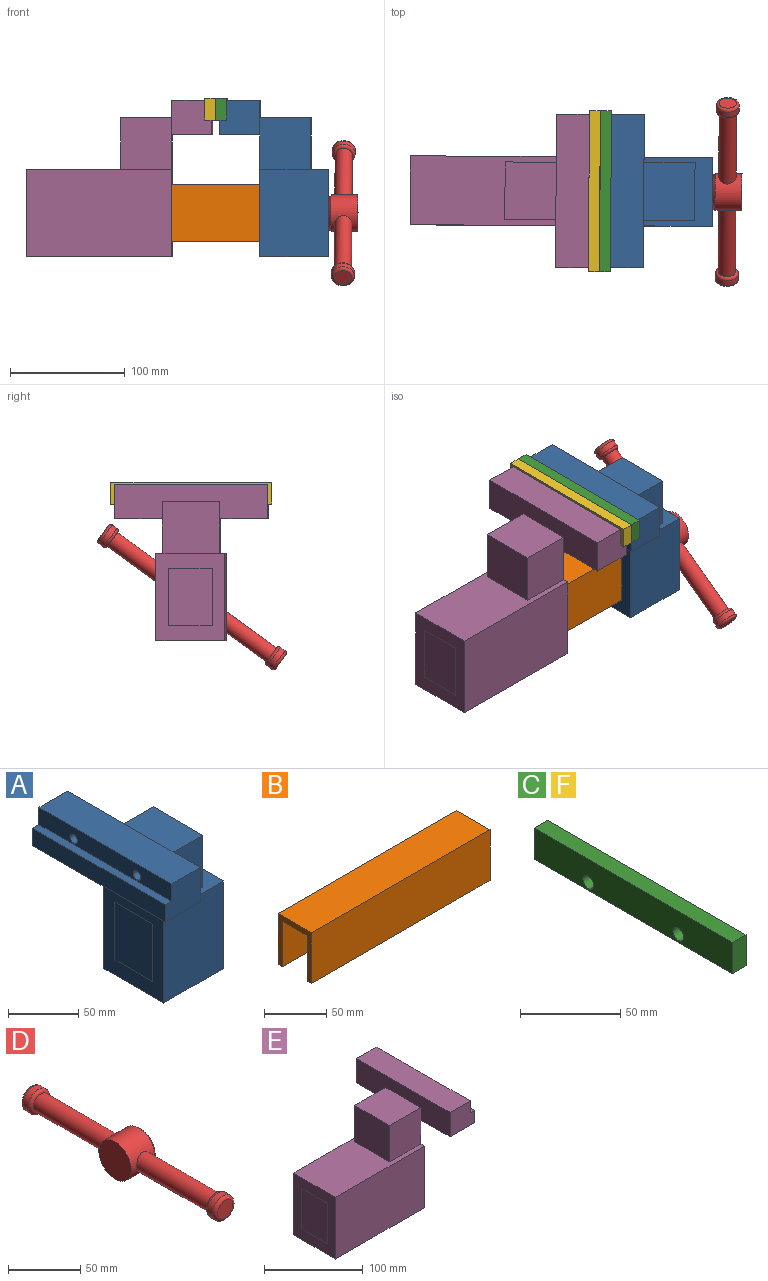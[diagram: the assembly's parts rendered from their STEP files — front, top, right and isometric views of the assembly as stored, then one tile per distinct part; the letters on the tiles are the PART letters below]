
ASSEMBLY  parts=6 mates=5
PART A: 28 faces, bbox 95x133.4x136.2 mm
  f0: plane 35x30mm, normal (0,1,0), area 954.8mm2, adj f11,f12,f13,f14,f16,f17
  f1: plane 106.2x60mm, normal (-1,0,0), area 6072mm2, adj f2,f4,f5,f6,f7,f9,f11
  f2: plane 60x60mm, normal (0,0,1), area 1377.5mm2, adj f1,f3,f5,f6,f7,f8,f9
  f3: plane 76.2x60mm, normal (1,0,0), area 4572mm2, adj f2,f4,f5,f6
  f4: plane 60x60mm, normal (0,0,-1), area 3600mm2, adj f1,f3,f5,f6
  f5: plane 76.2x60mm, normal (0,-1,0), area 4572mm2, adj f1,f2,f3,f4
  f6: plane 76.2x60mm, normal (0,1,0), area 4572mm2, adj f1,f2,f3,f4
  f7: plane 45x44.45mm, normal (0,1,0), area 2000.2mm2, adj f1,f2,f8,f10,f12
  f8: plane 50x45mm, normal (1,0,0), area 2250mm2, adj f2,f7,f9,f10
  f9: plane 45x44.45mm, normal (0,-1,0), area 2000.2mm2, adj f1,f2,f8,f10,f12
  f10: plane 50x44.45mm, normal (0,0,1), area 2222.5mm2, adj f7,f8,f9,f12
  f11: plane 133.35x35mm, normal (0,0,-1), area 4667.2mm2, adj f0,f1,f12,f14,f15
  f12: plane 133.35x30mm, normal (1,0,0), area 3250.5mm2, adj f0,f7,f9,f10,f11,f13,f15
  f13: plane 133.35x28.65mm, normal (0,0,1), area 3820.5mm2, adj f0,f12,f15,f17
  f14: plane 133.35x15mm, normal (-1,0,0), area 2000.2mm2, adj f0,f11,f15,f16
  f15: plane 35x30mm, normal (0,-1,0), area 954.8mm2, adj f11,f12,f13,f14,f16,f17
  f16: plane 133.35x6.35mm, normal (0,0,1), area 846.8mm2, adj f0,f14,f15,f17
  f17: plane 133.35x15mm, normal (-1,0,0), area 1911.9mm2, adj f0,f13,f15,f16,f19,f21
  f18: cone r=0mm half-angle=59deg, axis (-1,0,0), area 51.5mm2, adj f19
  f19: cylinder r=3.75mm len=10mm, axis (-1,0,0), area 235.6mm2, adj f17,f18
  f20: cone r=0mm half-angle=59deg, axis (-1,0,0), area 51.5mm2, adj f21
  f21: cylinder r=3.75mm len=10mm, axis (-1,0,0), area 235.6mm2, adj f17,f20
  f22: plane 50x38.11mm, normal (-1,0,0), area 1905.3mm2, adj f23,f24,f25,f26
  f23: plane 59.8x38.11mm, normal (0,0,1), area 2278.7mm2, adj f22,f25,f26,f27
  f24: plane 59.8x38.11mm, normal (0,0,-1), area 2278.7mm2, adj f22,f25,f26,f27
  f25: plane 59.8x50mm, normal (0,-1,0), area 2990mm2, adj f22,f23,f24,f27
  f26: plane 59.8x50mm, normal (0,1,0), area 2990mm2, adj f22,f23,f24,f27
  f27: plane 50x38.11mm, normal (1,0,0), area 1905.3mm2, adj f23,f24,f25,f26
PART B: 10 faces, bbox 203.4x38.1x50 mm
  f0: plane 203.36x5mm, normal (0,0,-1), area 1016.8mm2, adj f1,f3,f6,f9
  f1: plane 50x38.1mm, normal (1,0,0), area 640.5mm2, adj f0,f2,f4,f5,f6,f7,f8,f9
  f2: plane 203.36x5mm, normal (0,0,-1), area 1016.8mm2, adj f1,f3,f4,f7
  f3: plane 50x38.1mm, normal (-1,0,0), area 640.5mm2, adj f0,f2,f4,f5,f6,f7,f8,f9
  f4: plane 203.36x45mm, normal (0,1,0), area 9151.2mm2, adj f1,f2,f3,f5
  f5: plane 203.36x28.1mm, normal (0,0,-1), area 5714.4mm2, adj f1,f3,f4,f6
  f6: plane 203.36x45mm, normal (0,-1,0), area 9151.2mm2, adj f0,f1,f3,f5
  f7: plane 203.36x50mm, normal (0,-1,0), area 10168mm2, adj f1,f2,f3,f8
  f8: plane 203.36x38.1mm, normal (0,0,1), area 7748mm2, adj f1,f3,f7,f9
  f9: plane 203.36x50mm, normal (0,1,0), area 10168mm2, adj f0,f1,f3,f8
PART C: 8 faces, bbox 9.5x140x19.1 mm
  f0: plane 140x9.53mm, normal (0,0,1), area 1333.5mm2, adj f1,f3,f4,f6
  f1: plane 140x19.05mm, normal (-1,0,0), area 2578.6mm2, adj f0,f2,f4,f5,f6,f7
  f2: plane 140x9.53mm, normal (0,0,-1), area 1333.5mm2, adj f1,f3,f4,f6
  f3: plane 140x19.05mm, normal (1,0,0), area 2578.6mm2, adj f0,f2,f4,f5,f6,f7
  f4: plane 19.05x9.53mm, normal (0,-1,0), area 181.5mm2, adj f0,f1,f2,f3
  f5: cylinder r=3.75mm len=9.53mm, axis (1,0,0), area 224.4mm2, adj f1,f3
  f6: plane 19.05x9.53mm, normal (0,1,0), area 181.5mm2, adj f0,f1,f2,f3
  f7: cylinder r=3.75mm len=9.53mm, axis (1,0,0), area 224.4mm2, adj f1,f3
PART D: 14 faces, bbox 25.4x191x31.8 mm
  f0: cylinder r=15.88mm len=31.75mm, axis (-1,0,0), area 1968.9mm2, adj f2,f3,f4,f9
  f1: plane 27.75x27.75mm, normal (1,0,0), area 604.8mm2, adj f3
  f2: plane 31.75x31.75mm, normal (-1,0,0), area 791.7mm2, adj f0
  f3: cone r=13.88mm half-angle=45deg, axis (-1,0,0), area 264.4mm2, adj f0,f1
  f4: cylinder r=7.5mm len=71.51mm, axis (0,1,0), area 3324.6mm2, adj f0,f7
  f5: cylinder r=10mm len=20mm, axis (0,1,0), area 314.2mm2, adj f7,f8
  f6: plane 15x15mm, normal (0,-1,0), area 176.7mm2, adj f8
  f7: torus R=7.5mm, axis (0,-1,0), area 224.3mm2, adj f4,f5
  f8: torus R=7.5mm, axis (0,-1,0), area 224.3mm2, adj f5,f6
  f9: cylinder r=7.5mm len=71.51mm, axis (0,-1,0), area 3324.6mm2, adj f0,f12
  f10: cylinder r=10mm len=20mm, axis (0,-1,0), area 314.2mm2, adj f12,f13
  f11: plane 15x15mm, normal (0,1,0), area 176.7mm2, adj f13
  f12: torus R=7.5mm, axis (0,1,0), area 224.3mm2, adj f9,f10
  f13: torus R=7.5mm, axis (0,1,0), area 224.3mm2, adj f10,f11
PART E: 27 faces, bbox 162x133.4x136.2 mm
  f0: plane 133.35x15mm, normal (1,0,0), area 2000.2mm2, adj f1,f2,f19,f21
  f1: plane 35x30mm, normal (0,-1,0), area 954.8mm2, adj f0,f17,f18,f19,f20,f21
  f2: plane 35x30mm, normal (0,1,0), area 954.8mm2, adj f0,f17,f18,f19,f20,f21
  f3: plane 127x60mm, normal (0,0,1), area 5397.5mm2, adj f5,f6,f8,f12,f13,f14,f15
  f4: plane 126.9x50mm, normal (0,1,0), area 6345mm2, adj f5,f9,f10,f26
  f5: plane 106.2x60mm, normal (1,0,0), area 4166.7mm2, adj f3,f4,f7,f8,f9,f10,f11,f12
  f6: plane 76.2x60mm, normal (-1,0,0), area 4572mm2, adj f3,f7,f8,f12
  f7: plane 127x60mm, normal (0,0,-1), area 7620mm2, adj f5,f6,f8,f12
  f8: plane 127x76.2mm, normal (0,-1,0), area 9677.4mm2, adj f3,f5,f6,f7
  f9: plane 126.9x38.11mm, normal (0,0,-1), area 4835.5mm2, adj f4,f5,f11,f26
  f10: plane 126.9x38.11mm, normal (0,0,1), area 4835.5mm2, adj f4,f5,f11,f26
  f11: plane 126.9x50mm, normal (0,-1,0), area 6345mm2, adj f5,f9,f10,f26
  f12: plane 127x76.2mm, normal (0,1,0), area 9677.4mm2, adj f3,f5,f6,f7
  f13: plane 45x44.45mm, normal (0,-1,0), area 2000.2mm2, adj f3,f5,f15,f16,f18
  f14: plane 45x44.45mm, normal (0,1,0), area 2000.2mm2, adj f3,f5,f15,f16,f18
  f15: plane 50x45mm, normal (-1,0,0), area 2250mm2, adj f3,f13,f14,f16
  f16: plane 50x44.45mm, normal (0,0,1), area 2222.5mm2, adj f13,f14,f15,f18
  f17: plane 133.35x28.65mm, normal (0,0,1), area 3820.5mm2, adj f1,f2,f18,f20
  f18: plane 133.35x30mm, normal (-1,0,0), area 3250.5mm2, adj f1,f2,f13,f14,f16,f17,f19
  f19: plane 133.35x35mm, normal (0,0,-1), area 4667.2mm2, adj f0,f1,f2,f5,f18
  f20: plane 133.35x15mm, normal (1,0,0), area 1911.9mm2, adj f1,f2,f17,f21,f23,f25
  f21: plane 133.35x6.35mm, normal (0,0,1), area 846.8mm2, adj f0,f1,f2,f20
  f22: cone r=0mm half-angle=59deg, axis (1,0,0), area 51.5mm2, adj f23
  f23: cylinder r=3.75mm len=10mm, axis (1,0,0), area 235.6mm2, adj f20,f22
  f24: cone r=0mm half-angle=59deg, axis (1,0,0), area 51.5mm2, adj f25
  f25: cylinder r=3.75mm len=10mm, axis (1,0,0), area 235.6mm2, adj f20,f24
  f26: plane 50x38.11mm, normal (1,0,0), area 1905.3mm2, adj f4,f9,f10,f11
PART F: same geometry as C
PLACE A rot(axis=(0,0,-1),0.3deg) t=(-17.52,-35.09,19.33)mm
PLACE B rot(axis=(0,0,-1),0.3deg) t=(42.48,-35.41,19.39)mm
PLACE C rot(axis=(0,0,-1),0.3deg) t=(-50.93,-34.92,109.89)mm
PLACE D rot(axis=(0,-0.31,0.95),179.7deg) t=(127.88,-35.86,19.33)mm
PLACE E rot(axis=(0,0,-1),0.3deg) t=(-93.98,-34.69,19.39)mm fixed
PLACE F rot(axis=(0,0,-1),0.3deg) t=(-60.56,-34.87,109.95)mm
MATE revolute D.f0 <-> A.f3  axis (-1,0.01,0) through (42.48,-35.41,19.33)mm
MATE fastened E.f20 <-> F.f1  axis (1,-0.01,0) through (-65.33,-34.85,110.11)mm
MATE slider B.f3 <-> E.f26  axis (-1,0.01,0) through (-160.77,-15.29,44.39)mm
MATE fastened A.f17 <-> C.f3  axis (-1,0.01,0) through (-46.17,-34.94,110.04)mm
MATE fastened B.f1 <-> A.f3  axis (1,-0.01,0) through (42.48,-35.41,24.33)mm
